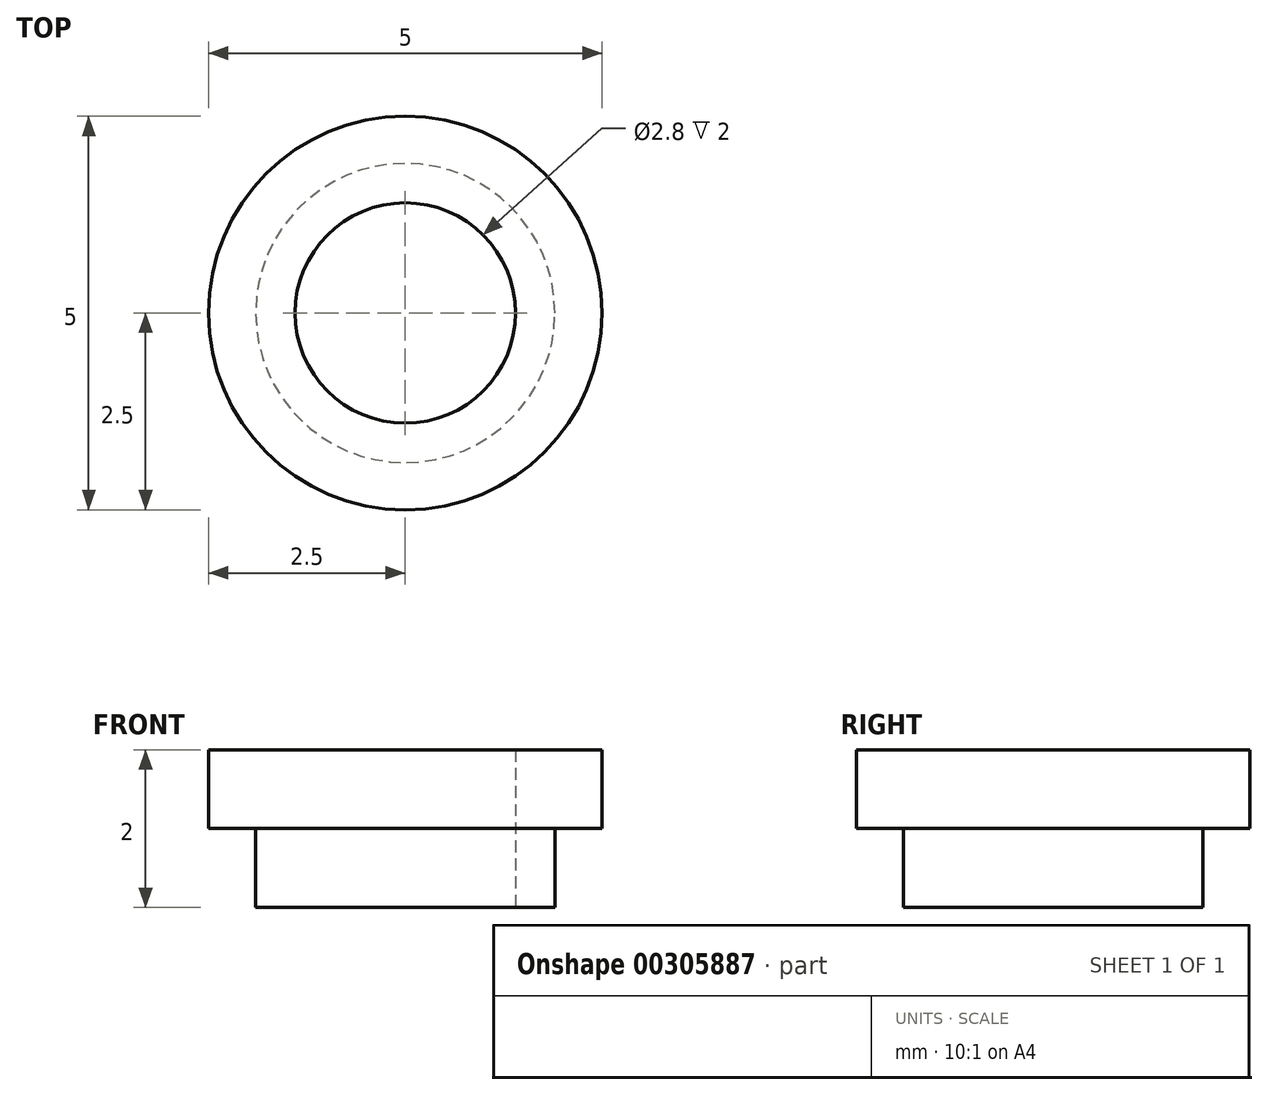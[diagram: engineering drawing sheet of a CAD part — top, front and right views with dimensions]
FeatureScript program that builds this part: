
annotation { "Feature Type Name" : "Feature", "Feature Type Description" : "" }
export const myFeature = defineFeature(function(context is Context, id is Id, definition is map)
    precondition{}
    {
        {
            var Q0;
            Q0=qCreatedBy(makeId("Top.planeOp"),FACE);
            var sketch = newSketch(context, id + "F0", { "sketchPlane" : qUnion([Q0])});
            skCircle(sketch, "E0", {"center": v(0, 0) * mm, "radius": 1.9 * mm});
            skCircle(sketch, "E1", {"center": v(0, 0) * mm, "radius": 1.4 * mm});
            skSolve(sketch);
        }
        {
            var Q0;
            Q0=makeQuery(id+"F0.imprint","IMPRINT",FACE,{"disambiguationData":[TD([[makeQuery(id+"F0.imprint","IMPRINT",EDGE,{"derivedFrom":sQuery(id+"F0.wireOp",EDGE,"E0")}),1.0]])]});
            extrude(context, id + "F1", {"entities" : qUnion([Q0]), "depth" : 1 * mm});
        }
        {
            var Q0;
            Q0=makeQuery(id+"F1.opExtrude","CAP_FACE",FACE,{"disambiguationData":[OSD([sQuery(id+"F0.wireOp",EDGE,"E0"),sQuery(id+"F0.wireOp",EDGE,"E1")])],"isStart":false});
            var sketch = newSketch(context, id + "F2", { "sketchPlane" : qUnion([Q0])});
            skCircle(sketch, "E2", {"center": v(0, 0) * mm, "radius": 2.5 * mm});
            skCircle(sketch, "E3.0", {"center": v(0, 0) * mm, "radius": 1.4 * mm});
            skSolve(sketch);
        }
        {
            var Q0;
            Q0 = qSketchRegion(id + "F2", true);
            extrude(context, id + "F3", {"entities" : qUnion([Q0]), "operationType" : NewBodyOperationType.ADD, "depth" : 1 * mm});
        }
    });
